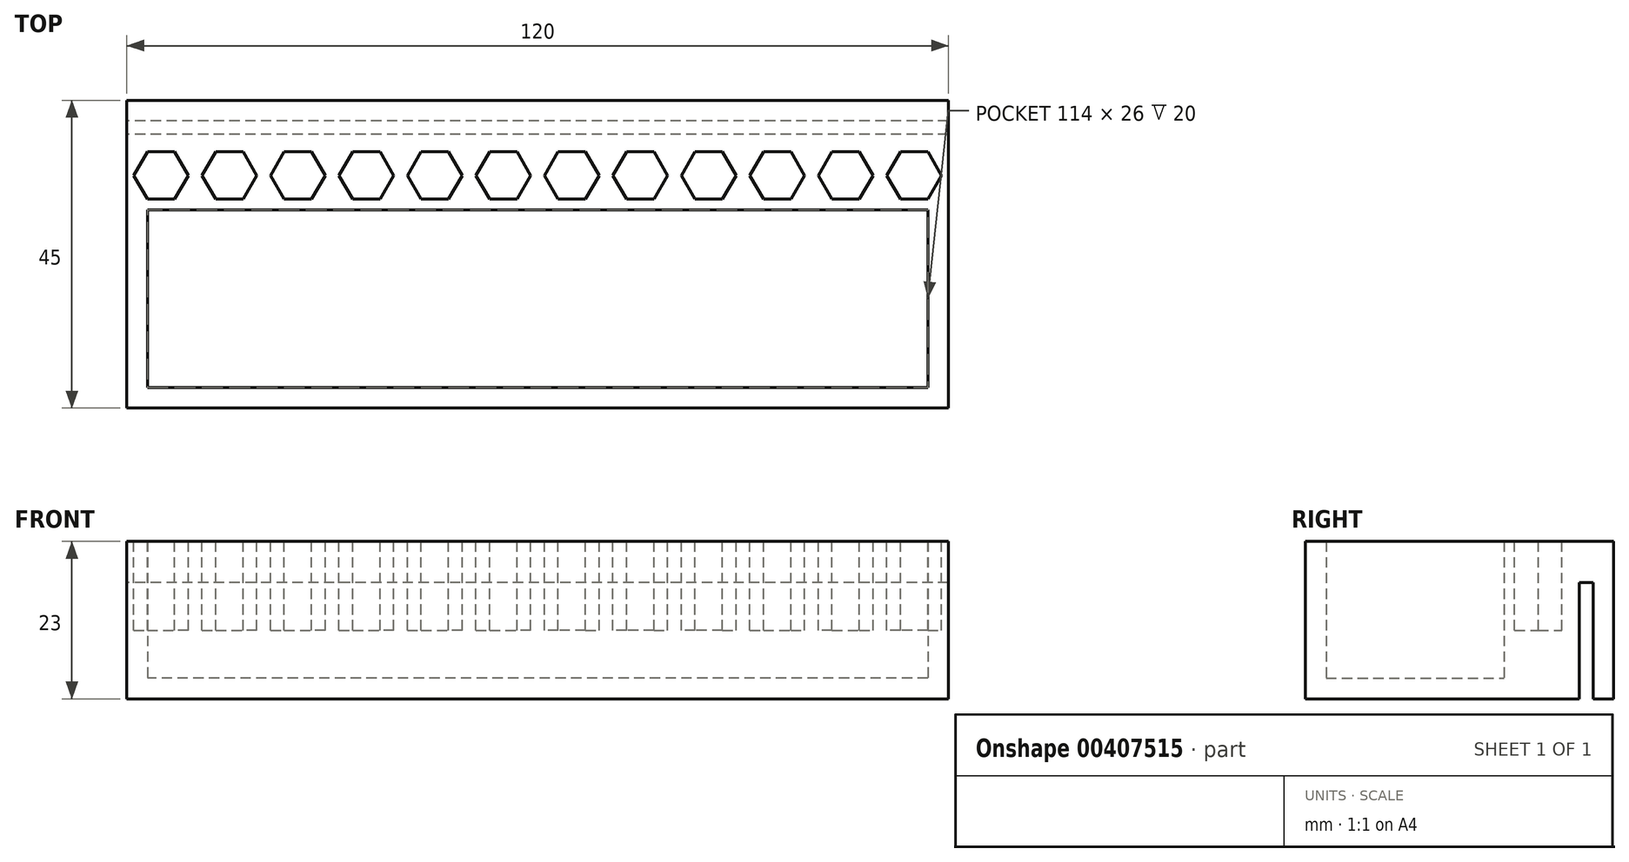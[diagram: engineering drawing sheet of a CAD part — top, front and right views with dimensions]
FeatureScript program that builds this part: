
annotation { "Feature Type Name" : "Feature", "Feature Type Description" : "" }
export const myFeature = defineFeature(function(context is Context, id is Id, definition is map)
    precondition{}
    {
        {
            var Q0;
            Q0=qCreatedBy(makeId("Top.planeOp"),FACE);
            var sketch = newSketch(context, id + "F0", { "sketchPlane" : qUnion([Q0])});
            skLineSegment(sketch, "E0.bottom", {"start": v(60, -22.5) * mm, "end": v(-60, -22.5) * mm});
            skLineSegment(sketch, "E0.top", {"start": v(60, 22.5) * mm, "end": v(-60, 22.5) * mm});
            skLineSegment(sketch, "E0.left", {"start": v(60, -22.5) * mm, "end": v(60, 22.5) * mm});
            skLineSegment(sketch, "E0.right", {"start": v(-60, -22.5) * mm, "end": v(-60, 22.5) * mm});
            skPoint(sketch, "E0.middle", {"position": v(0, 0) * mm});
            skPoint(sketch, "E1.middle", {"position": v(0, 26) * mm});
            skPoint(sketch, "E1.middle.positionSnap0", {"position": v(0, 22.5) * mm});
            skPoint(sketch, "E1.centerSnap0", {"position": v(0, 22.5) * mm});
            skSolve(sketch);
        }
        {
            var Q0;
            Q0=makeQuery(id+"F0.imprint","IMPRINT",FACE,{"disambiguationData":[TD([[makeQuery(id+"F0.imprint","IMPRINT",EDGE,{"derivedFrom":sQuery(id+"F0.wireOp",EDGE,"E0.bottom")}),-1.0]])]});
            extrude(context, id + "F1", {"entities" : qUnion([Q0]), "depth" : 3 * mm});
        }
        {
            var Q0;
            Q0=makeQuery(id+"F1.opExtrude","CAP_FACE",FACE,{"disambiguationData":[OSD([sQuery(id+"F0.wireOp",EDGE,"E0.bottom"),sQuery(id+"F0.wireOp",EDGE,"E0.top"),sQuery(id+"F0.wireOp",EDGE,"E0.left"),sQuery(id+"F0.wireOp",EDGE,"E0.right")])],"isStart":false});
            var sketch = newSketch(context, id + "F2", { "sketchPlane" : qUnion([Q0])});
            skLineSegment(sketch, "E2.bottom", {"start": v(57, -19.5) * mm, "end": v(-57, -19.5) * mm});
            skLineSegment(sketch, "E2.top", {"start": v(57, 6.5) * mm, "end": v(-57, 6.5) * mm});
            skLineSegment(sketch, "E2.left", {"start": v(57, -19.5) * mm, "end": v(57, 6.5) * mm});
            skLineSegment(sketch, "E2.right", {"start": v(-57, -19.5) * mm, "end": v(-57, 6.5) * mm});
            skPoint(sketch, "E2.middle", {"position": v(0, 0) * mm});
            skSolve(sketch);
        }
        {
            var Q0;
            Q0=makeQuery(id+"F2.imprint","IMPRINT",FACE,{"disambiguationData":[TD([[makeQuery(id+"F2.imprint","IMPRINT",EDGE,{"derivedFrom":sQuery(id+"F2.wireOp",EDGE,"E2.bottom")}),1.0]])]});
            extrude(context, id + "F3", {"entities" : qUnion([Q0]), "operationType" : NewBodyOperationType.ADD, "depth" : 20 * mm});
        }
        {
            var Q0;
            Q0=makeQuery(id+"F3.opExtrude","CAP_FACE",FACE,{"disambiguationData":[OSD([sQuery(id+"F0.wireOp",EDGE,"E0.bottom"),sQuery(id+"F0.wireOp",EDGE,"E0.top"),sQuery(id+"F0.wireOp",EDGE,"E0.left"),sQuery(id+"F0.wireOp",EDGE,"E0.right"),sQuery(id+"F2.wireOp",EDGE,"E2.bottom"),sQuery(id+"F2.wireOp",EDGE,"E2.top"),sQuery(id+"F2.wireOp",EDGE,"E2.left"),sQuery(id+"F2.wireOp",EDGE,"E2.right")])],"isStart":false});
            var sketch = newSketch(context, id + "F4", { "sketchPlane" : qUnion([Q0])});
            skLineSegment(sketch, "E3", {"start": v(-60, 11.5) * mm, "end": v(60, 11.5) * mm, "construction": true});
            skCircle(sketch, "E4.cCircle", {"center": v(-55, 11.5) * mm, "radius": 4 * mm, "construction": true});
            skLineSegment(sketch, "E4.0", {"start": v(-51, 11.5) * mm, "end": v(-53, 8.04) * mm});
            skLineSegment(sketch, "E4.1", {"start": v(-53, 8.04) * mm, "end": v(-57, 8.04) * mm});
            skLineSegment(sketch, "E4.2", {"start": v(-57, 8.04) * mm, "end": v(-59, 11.5) * mm});
            skLineSegment(sketch, "E4.3", {"start": v(-59, 11.5) * mm, "end": v(-57, 14.96) * mm});
            skLineSegment(sketch, "E4.4", {"start": v(-57, 14.96) * mm, "end": v(-53, 14.96) * mm});
            skLineSegment(sketch, "E4.5", {"start": v(-53, 14.96) * mm, "end": v(-51, 11.5) * mm});
            skCircle(sketch, "E5.cCircle", {"center": v(-45, 11.5) * mm, "radius": 4 * mm, "construction": true});
            skLineSegment(sketch, "E5.0", {"start": v(-41, 11.5) * mm, "end": v(-43, 8.04) * mm});
            skLineSegment(sketch, "E5.1", {"start": v(-43, 8.04) * mm, "end": v(-47, 8.04) * mm});
            skLineSegment(sketch, "E5.2", {"start": v(-47, 8.04) * mm, "end": v(-49, 11.5) * mm});
            skLineSegment(sketch, "E5.3", {"start": v(-49, 11.5) * mm, "end": v(-47, 14.96) * mm});
            skLineSegment(sketch, "E5.4", {"start": v(-47, 14.96) * mm, "end": v(-43, 14.96) * mm});
            skLineSegment(sketch, "E5.5", {"start": v(-43, 14.96) * mm, "end": v(-41, 11.5) * mm});
            skCircle(sketch, "E6.cCircle", {"center": v(-35, 11.5) * mm, "radius": 4 * mm, "construction": true});
            skLineSegment(sketch, "E6.0", {"start": v(-31, 11.5) * mm, "end": v(-33, 8.04) * mm});
            skLineSegment(sketch, "E6.1", {"start": v(-33, 8.04) * mm, "end": v(-37, 8.04) * mm});
            skLineSegment(sketch, "E6.2", {"start": v(-37, 8.04) * mm, "end": v(-39, 11.5) * mm});
            skLineSegment(sketch, "E6.3", {"start": v(-39, 11.5) * mm, "end": v(-37, 14.96) * mm});
            skLineSegment(sketch, "E6.4", {"start": v(-37, 14.96) * mm, "end": v(-33, 14.96) * mm});
            skLineSegment(sketch, "E6.5", {"start": v(-33, 14.96) * mm, "end": v(-31, 11.5) * mm});
            skCircle(sketch, "E7.cCircle", {"center": v(-5, 11.5) * mm, "radius": 4 * mm, "construction": true});
            skLineSegment(sketch, "E7.0", {"start": v(-1, 11.5) * mm, "end": v(-3, 8.04) * mm});
            skLineSegment(sketch, "E7.1", {"start": v(-3, 8.04) * mm, "end": v(-7, 8.04) * mm});
            skLineSegment(sketch, "E7.2", {"start": v(-7, 8.04) * mm, "end": v(-9, 11.5) * mm});
            skLineSegment(sketch, "E7.3", {"start": v(-9, 11.5) * mm, "end": v(-7, 14.96) * mm});
            skLineSegment(sketch, "E7.4", {"start": v(-7, 14.96) * mm, "end": v(-3, 14.96) * mm});
            skLineSegment(sketch, "E7.5", {"start": v(-3, 14.96) * mm, "end": v(-1, 11.5) * mm});
            skCircle(sketch, "E8.cCircle", {"center": v(-15, 11.5) * mm, "radius": 4 * mm, "construction": true});
            skLineSegment(sketch, "E8.0", {"start": v(-11, 11.5) * mm, "end": v(-13, 8.04) * mm});
            skLineSegment(sketch, "E8.1", {"start": v(-13, 8.04) * mm, "end": v(-17, 8.04) * mm});
            skLineSegment(sketch, "E8.2", {"start": v(-17, 8.04) * mm, "end": v(-19, 11.5) * mm});
            skLineSegment(sketch, "E8.3", {"start": v(-19, 11.5) * mm, "end": v(-17, 14.96) * mm});
            skLineSegment(sketch, "E8.4", {"start": v(-17, 14.96) * mm, "end": v(-13, 14.96) * mm});
            skLineSegment(sketch, "E8.5", {"start": v(-13, 14.96) * mm, "end": v(-11, 11.5) * mm});
            skCircle(sketch, "E9.cCircle", {"center": v(-25, 11.5) * mm, "radius": 4 * mm, "construction": true});
            skLineSegment(sketch, "E9.0", {"start": v(-21, 11.5) * mm, "end": v(-23, 8.04) * mm});
            skLineSegment(sketch, "E9.1", {"start": v(-23, 8.04) * mm, "end": v(-27, 8.04) * mm});
            skLineSegment(sketch, "E9.2", {"start": v(-27, 8.04) * mm, "end": v(-29, 11.5) * mm});
            skLineSegment(sketch, "E9.3", {"start": v(-29, 11.5) * mm, "end": v(-27, 14.96) * mm});
            skLineSegment(sketch, "E9.4", {"start": v(-27, 14.96) * mm, "end": v(-23, 14.96) * mm});
            skLineSegment(sketch, "E9.5", {"start": v(-23, 14.96) * mm, "end": v(-21, 11.5) * mm});
            skLineSegment(sketch, "E10.MirrorCS", {"start": v(27, 14.96) * mm, "end": v(23, 14.96) * mm});
            skLineSegment(sketch, "E11.MirrorCS", {"start": v(7, 8.04) * mm, "end": v(9, 11.5) * mm});
            skLineSegment(sketch, "E12.MirrorCS", {"start": v(23, 8.04) * mm, "end": v(27, 8.04) * mm});
            skLineSegment(sketch, "E13.MirrorCS", {"start": v(13, 8.04) * mm, "end": v(17, 8.04) * mm});
            skCircle(sketch, "E14.MirrorC", {"center": v(5, 11.5) * mm, "radius": 4 * mm, "construction": true});
            skLineSegment(sketch, "E15.MirrorCS", {"start": v(17, 14.96) * mm, "end": v(13, 14.96) * mm});
            skLineSegment(sketch, "E16.MirrorCS", {"start": v(37, 8.04) * mm, "end": v(39, 11.5) * mm});
            skLineSegment(sketch, "E17.MirrorCS", {"start": v(23, 14.96) * mm, "end": v(21, 11.5) * mm});
            skLineSegment(sketch, "E18.MirrorCS", {"start": v(9, 11.5) * mm, "end": v(7, 14.96) * mm});
            skLineSegment(sketch, "E19.MirrorCS", {"start": v(13, 14.96) * mm, "end": v(11, 11.5) * mm});
            skLineSegment(sketch, "E20.MirrorCS", {"start": v(39, 11.5) * mm, "end": v(37, 14.96) * mm});
            skLineSegment(sketch, "E21.MirrorCS", {"start": v(33, 8.04) * mm, "end": v(37, 8.04) * mm});
            skLineSegment(sketch, "E22.MirrorCS", {"start": v(19, 11.5) * mm, "end": v(17, 14.96) * mm});
            skLineSegment(sketch, "E23.MirrorCS", {"start": v(33, 14.96) * mm, "end": v(31, 11.5) * mm});
            skLineSegment(sketch, "E24.MirrorCS", {"start": v(3, 14.96) * mm, "end": v(1, 11.5) * mm});
            skLineSegment(sketch, "E25.MirrorCS", {"start": v(47, 8.04) * mm, "end": v(49, 11.5) * mm});
            skLineSegment(sketch, "E26.MirrorCS", {"start": v(49, 11.5) * mm, "end": v(47, 14.96) * mm});
            skLineSegment(sketch, "E27.MirrorCS", {"start": v(17, 8.04) * mm, "end": v(19, 11.5) * mm});
            skLineSegment(sketch, "E28.MirrorCS", {"start": v(31, 11.5) * mm, "end": v(33, 8.04) * mm});
            skLineSegment(sketch, "E29.MirrorCS", {"start": v(29, 11.5) * mm, "end": v(27, 14.96) * mm});
            skLineSegment(sketch, "E30.MirrorCS", {"start": v(7, 14.96) * mm, "end": v(3, 14.96) * mm});
            skLineSegment(sketch, "E31.MirrorCS", {"start": v(1, 11.5) * mm, "end": v(3, 8.04) * mm});
            skLineSegment(sketch, "E32.MirrorCS", {"start": v(59, 11.5) * mm, "end": v(57, 14.96) * mm});
            skLineSegment(sketch, "E33.MirrorCS", {"start": v(27, 8.04) * mm, "end": v(29, 11.5) * mm});
            skCircle(sketch, "E34.MirrorC", {"center": v(55, 11.5) * mm, "radius": 4 * mm, "construction": true});
            skCircle(sketch, "E35.MirrorC", {"center": v(25, 11.5) * mm, "radius": 4 * mm, "construction": true});
            skLineSegment(sketch, "E36.MirrorCS", {"start": v(37, 14.96) * mm, "end": v(33, 14.96) * mm});
            skLineSegment(sketch, "E37.MirrorCS", {"start": v(43, 8.04) * mm, "end": v(47, 8.04) * mm});
            skLineSegment(sketch, "E38.MirrorCS", {"start": v(47, 14.96) * mm, "end": v(43, 14.96) * mm});
            skLineSegment(sketch, "E39.MirrorCS", {"start": v(41, 11.5) * mm, "end": v(43, 8.04) * mm});
            skLineSegment(sketch, "E40.MirrorCS", {"start": v(53, 14.96) * mm, "end": v(51, 11.5) * mm});
            skLineSegment(sketch, "E41.MirrorCS", {"start": v(43, 14.96) * mm, "end": v(41, 11.5) * mm});
            skCircle(sketch, "E42.MirrorC", {"center": v(15, 11.5) * mm, "radius": 4 * mm, "construction": true});
            skCircle(sketch, "E43.MirrorC", {"center": v(45, 11.5) * mm, "radius": 4 * mm, "construction": true});
            skLineSegment(sketch, "E44.MirrorCS", {"start": v(11, 11.5) * mm, "end": v(13, 8.04) * mm});
            skCircle(sketch, "E45.MirrorC", {"center": v(35, 11.5) * mm, "radius": 4 * mm, "construction": true});
            skLineSegment(sketch, "E46.MirrorCS", {"start": v(3, 8.04) * mm, "end": v(7, 8.04) * mm});
            skLineSegment(sketch, "E47.MirrorCS", {"start": v(53, 8.04) * mm, "end": v(57, 8.04) * mm});
            skLineSegment(sketch, "E48.MirrorCS", {"start": v(57, 8.04) * mm, "end": v(59, 11.5) * mm});
            skLineSegment(sketch, "E49.MirrorCS", {"start": v(57, 14.96) * mm, "end": v(53, 14.96) * mm});
            skLineSegment(sketch, "E50.MirrorCS", {"start": v(51, 11.5) * mm, "end": v(53, 8.04) * mm});
            skLineSegment(sketch, "E51.MirrorCS", {"start": v(21, 11.5) * mm, "end": v(23, 8.04) * mm});
            skSolve(sketch);
        }
        {
            var Q0;
            Q0=makeQuery(id+"F1.opExtrude","CAP_FACE",FACE,{"disambiguationData":[OSD([sQuery(id+"F0.wireOp",EDGE,"E0.bottom"),sQuery(id+"F0.wireOp",EDGE,"E0.top"),sQuery(id+"F0.wireOp",EDGE,"E0.left"),sQuery(id+"F0.wireOp",EDGE,"E0.right")])],"isStart":true});
            var sketch = newSketch(context, id + "F5", { "sketchPlane" : qUnion([Q0])});
            skLineSegment(sketch, "E52", {"start": v(60, -19.5) * mm, "end": v(-60, -19.5) * mm});
            skLineSegment(sketch, "E53", {"start": v(60, -17.5) * mm, "end": v(-60, -17.5) * mm});
            skSolve(sketch);
        }
        {
            var Q0;
            {var subQ0=sQuery(id+"F5.wireOp",EDGE,"E52");Q0=makeQuery(id+"F5.imprint","IMPRINT",FACE,{"disambiguationData":[TD([[makeQuery(id+"F5.imprint","IMPRINT",EDGE,{"derivedFrom":subQ0}),-1.0]])]});}
            extrude(context, id + "F6", {"entities" : qUnion([Q0]), "operationType" : NewBodyOperationType.REMOVE, "oppositeDirection" : true, "depth" : 17 * mm});
        }
        {
            var Q0;
            Q0=makeQuery(id+"F4.imprint","IMPRINT",FACE,{"disambiguationData":[TD([[makeQuery(id+"F4.imprint","IMPRINT",EDGE,{"derivedFrom":sQuery(id+"F4.wireOp",EDGE,"E4.0")}),-1.0]])]});
            var Q1;
            Q1=makeQuery(id+"F4.imprint","IMPRINT",FACE,{"disambiguationData":[TD([[makeQuery(id+"F4.imprint","IMPRINT",EDGE,{"derivedFrom":sQuery(id+"F4.wireOp",EDGE,"E5.0")}),-1.0]])]});
            var Q2;
            Q2=makeQuery(id+"F4.imprint","IMPRINT",FACE,{"disambiguationData":[TD([[makeQuery(id+"F4.imprint","IMPRINT",EDGE,{"derivedFrom":sQuery(id+"F4.wireOp",EDGE,"E6.0")}),-1.0]])]});
            var Q3;
            Q3=makeQuery(id+"F4.imprint","IMPRINT",FACE,{"disambiguationData":[TD([[makeQuery(id+"F4.imprint","IMPRINT",EDGE,{"derivedFrom":sQuery(id+"F4.wireOp",EDGE,"E9.0")}),-1.0]])]});
            var Q4;
            Q4=makeQuery(id+"F4.imprint","IMPRINT",FACE,{"disambiguationData":[TD([[makeQuery(id+"F4.imprint","IMPRINT",EDGE,{"derivedFrom":sQuery(id+"F4.wireOp",EDGE,"E8.0")}),-1.0]])]});
            var Q5;
            Q5=makeQuery(id+"F4.imprint","IMPRINT",FACE,{"disambiguationData":[TD([[makeQuery(id+"F4.imprint","IMPRINT",EDGE,{"derivedFrom":sQuery(id+"F4.wireOp",EDGE,"E7.0")}),-1.0]])]});
            var Q6;
            Q6=makeQuery(id+"F4.imprint","IMPRINT",FACE,{"disambiguationData":[TD([[makeQuery(id+"F4.imprint","IMPRINT",EDGE,{"derivedFrom":sQuery(id+"F4.wireOp",EDGE,"E11.MirrorCS")}),1.0]])]});
            var Q7;
            Q7=makeQuery(id+"F4.imprint","IMPRINT",FACE,{"disambiguationData":[TD([[makeQuery(id+"F4.imprint","IMPRINT",EDGE,{"derivedFrom":sQuery(id+"F4.wireOp",EDGE,"E13.MirrorCS")}),1.0]])]});
            var Q8;
            Q8=makeQuery(id+"F4.imprint","IMPRINT",FACE,{"disambiguationData":[TD([[makeQuery(id+"F4.imprint","IMPRINT",EDGE,{"derivedFrom":sQuery(id+"F4.wireOp",EDGE,"E10.MirrorCS")}),1.0]])]});
            var Q9;
            Q9=makeQuery(id+"F4.imprint","IMPRINT",FACE,{"disambiguationData":[TD([[makeQuery(id+"F4.imprint","IMPRINT",EDGE,{"derivedFrom":sQuery(id+"F4.wireOp",EDGE,"E16.MirrorCS")}),1.0]])]});
            var Q10;
            Q10=makeQuery(id+"F4.imprint","IMPRINT",FACE,{"disambiguationData":[TD([[makeQuery(id+"F4.imprint","IMPRINT",EDGE,{"derivedFrom":sQuery(id+"F4.wireOp",EDGE,"E25.MirrorCS")}),1.0]])]});
            var Q11;
            Q11=makeQuery(id+"F4.imprint","IMPRINT",FACE,{"disambiguationData":[TD([[makeQuery(id+"F4.imprint","IMPRINT",EDGE,{"derivedFrom":sQuery(id+"F4.wireOp",EDGE,"E32.MirrorCS")}),1.0]])]});
            extrude(context, id + "F7", {"entities" : qUnion([Q0, Q1, Q2, Q3, Q4, Q5, Q6, Q7, Q8, Q9, Q10, Q11]), "operationType" : NewBodyOperationType.REMOVE, "oppositeDirection" : true, "depth" : 13 * mm});
        }
    });
